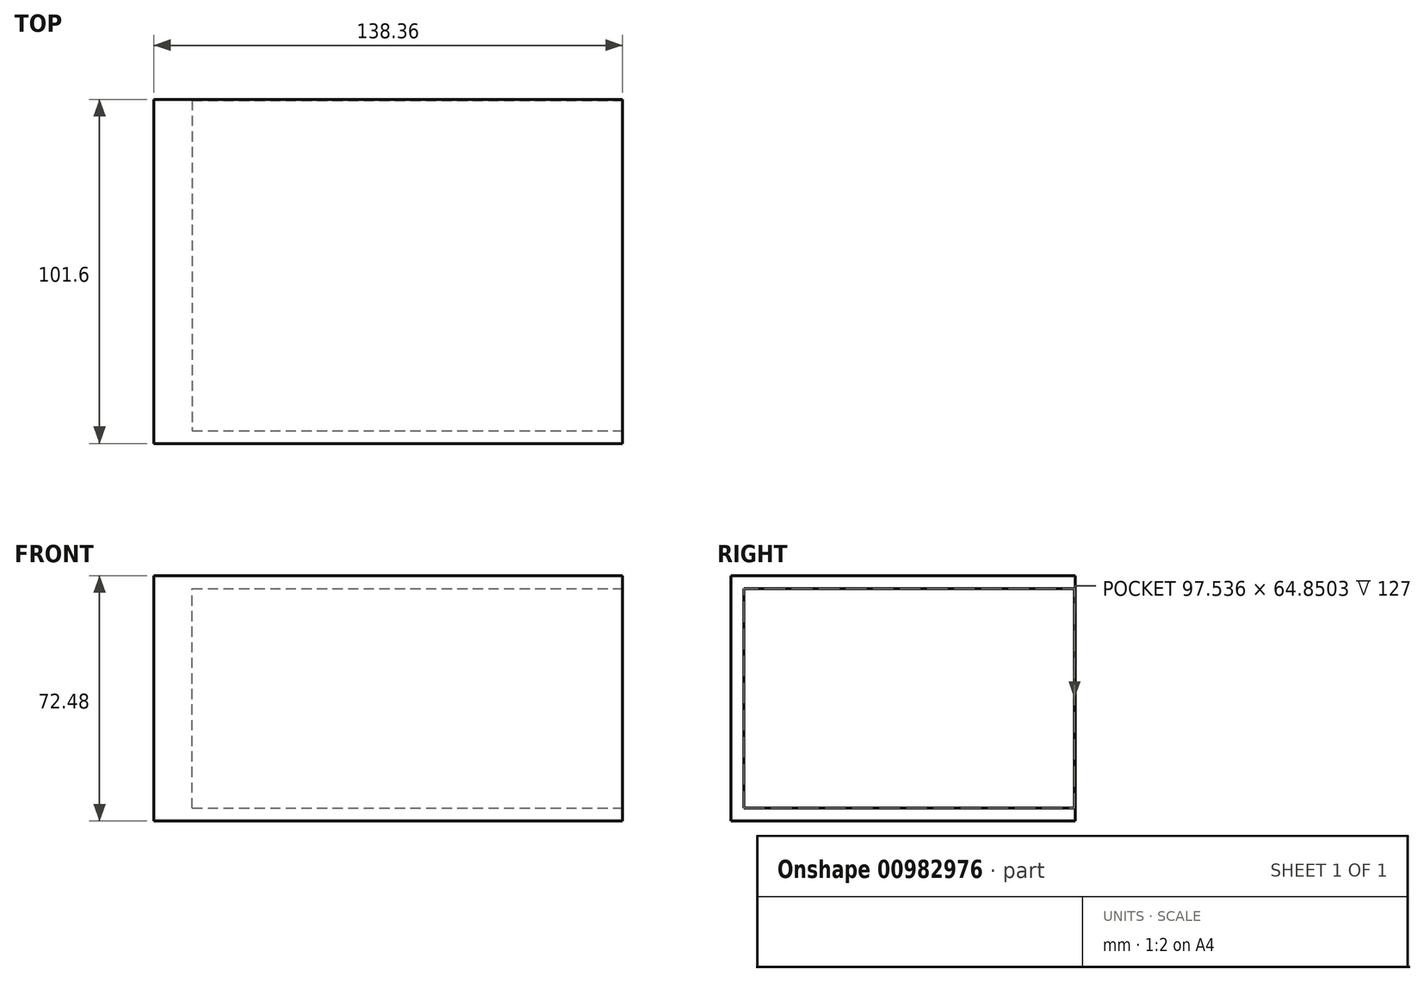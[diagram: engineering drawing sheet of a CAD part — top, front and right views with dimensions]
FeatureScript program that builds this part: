
annotation { "Feature Type Name" : "Feature", "Feature Type Description" : "" }
export const myFeature = defineFeature(function(context is Context, id is Id, definition is map)
    precondition{}
    {
        {
            var Q0;
            Q0=qCreatedBy(makeId("Front.planeOp"),FACE);
            var sketch = newSketch(context, id + "F0", { "sketchPlane" : qUnion([Q0])});
            skLineSegment(sketch, "E0", {"start": v(-47.37, 9.5) * mm, "end": v(90.99, 9.5) * mm});
            skLineSegment(sketch, "E1", {"start": v(90.99, 9.5) * mm, "end": v(90.99, 81.97) * mm});
            skLineSegment(sketch, "E2", {"start": v(90.99, 81.97) * mm, "end": v(-47.37, 81.97) * mm});
            skLineSegment(sketch, "E3", {"start": v(-47.37, 81.97) * mm, "end": v(-47.37, 9.5) * mm});
            skSolve(sketch);
        }
        {
            var Q0;
            Q0=makeQuery(id+"F0.imprint","IMPRINT",FACE,{"disambiguationData":[TD([[makeQuery(id+"F0.imprint","IMPRINT",EDGE,{"derivedFrom":sQuery(id+"F0.wireOp",EDGE,"E0")}),1.0]])]});
            extrude(context, id + "F1", {"entities" : qUnion([Q0]), "depth" : 101.6 * mm, "offsetDistance" : 25.4 * mm});
        }
        {
            var Q0;
            Q0=makeQuery(id+"F1.opExtrude","SWEPT_FACE",FACE,{"disambiguationData":[OSD([sQuery(id+"F0.wireOp",EDGE,"E1")])]});
            var sketch = newSketch(context, id + "F2", { "sketchPlane" : qUnion([Q0])});
            skPoint(sketch, "E4", {"position": v(0, 78.16) * mm});
            skPoint(sketch, "E5", {"position": v(0, 13.3) * mm});
            skLineSegment(sketch, "E6", {"start": v(0, 78.16) * mm, "end": v(-101.6, 78.16) * mm});
            skLineSegment(sketch, "E7", {"start": v(0, 13.3) * mm, "end": v(-101.6, 13.3) * mm});
            skPoint(sketch, "E8", {"position": v(-0.25, 13.3) * mm});
            skPoint(sketch, "E9", {"position": v(-97.8, 13.3) * mm});
            skLineSegment(sketch, "E10", {"start": v(-0.25, 13.3) * mm, "end": v(-0.25, 78.16) * mm});
            skLineSegment(sketch, "E11", {"start": v(-97.8, 13.3) * mm, "end": v(-97.8, 78.16) * mm});
            skSolve(sketch);
        }
        {
            var Q0;
            {var subQ0=sQuery(id+"F2.wireOp",EDGE,"E10");Q0=makeQuery(id+"F2.imprint","IMPRINT",FACE,{"disambiguationData":[TD([[makeQuery(id+"F2.imprint","IMPRINT",EDGE,{"derivedFrom":subQ0}),1.0]])]});}
            extrude(context, id + "F3", {"entities" : qUnion([Q0]), "operationType" : NewBodyOperationType.REMOVE, "oppositeDirection" : true, "depth" : 127 * mm, "offsetDistance" : 25.4 * mm});
        }
    });
